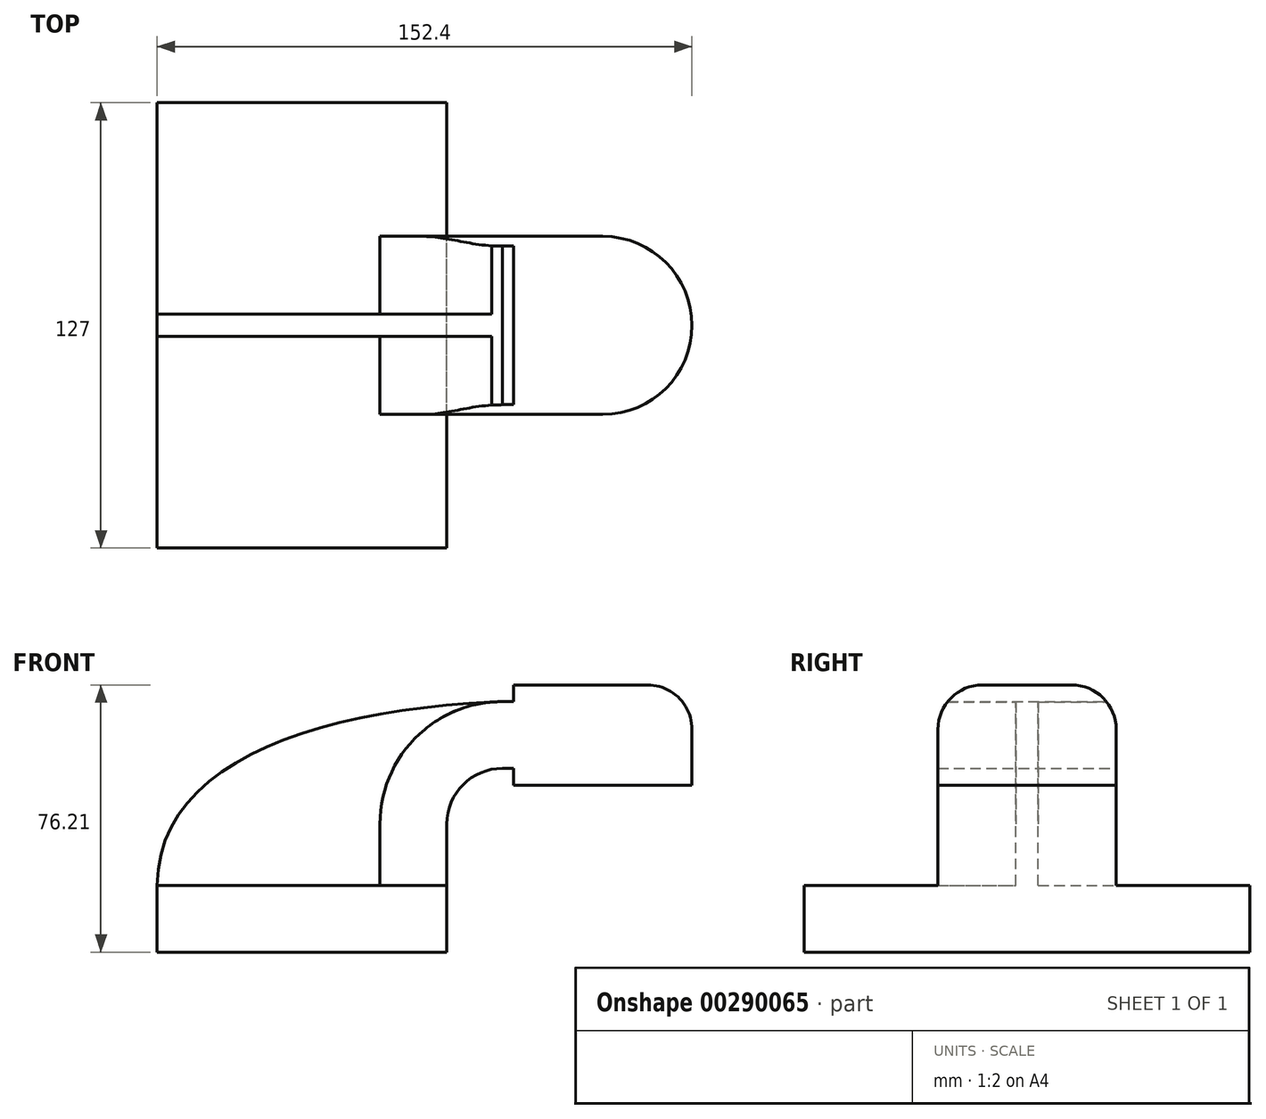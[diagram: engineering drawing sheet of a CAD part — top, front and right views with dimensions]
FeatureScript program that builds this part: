
annotation { "Feature Type Name" : "Feature", "Feature Type Description" : "" }
export const myFeature = defineFeature(function(context is Context, id is Id, definition is map)
    precondition{}
    {
        {
            var Q0;
            Q0=qCreatedBy(makeId("Front.planeOp"),FACE);
            var sketch = newSketch(context, id + "F0", { "sketchPlane" : qUnion([Q0])});
            skLineSegment(sketch, "E0.bottom", {"start": v(41.28, 9.52) * mm, "end": v(-41.28, 9.52) * mm});
            skLineSegment(sketch, "E0.top", {"start": v(41.28, -9.53) * mm, "end": v(-41.28, -9.53) * mm});
            skLineSegment(sketch, "E0.left", {"start": v(41.28, 9.52) * mm, "end": v(41.28, -9.53) * mm});
            skLineSegment(sketch, "E0.right", {"start": v(-41.28, 9.52) * mm, "end": v(-41.28, -9.53) * mm});
            skPoint(sketch, "E0.middle", {"position": v(0, 0) * mm});
            skLineSegment(sketch, "E1.bottom", {"start": v(60.33, 66.67) * mm, "end": v(111.13, 66.68) * mm});
            skLineSegment(sketch, "E1.top", {"start": v(60.33, 38.1) * mm, "end": v(111.13, 38.1) * mm});
            skLineSegment(sketch, "E1.left", {"start": v(60.33, 66.67) * mm, "end": v(60.33, 38.1) * mm});
            skLineSegment(sketch, "E1.right", {"start": v(111.13, 66.68) * mm, "end": v(111.13, 38.1) * mm});
            skPoint(sketch, "E1.middle", {"position": v(85.73, 52.39) * mm});
            skLineSegment(sketch, "E2", {"start": v(41.28, 9.52) * mm, "end": v(41.28, 27) * mm});
            skArc(sketch, "E3", {"start": v(41.28, 27) * mm, "mid": v(45.92, 38.23) * mm, "end": v(57.15, 42.88) * mm});
            skLineSegment(sketch, "E4", {"start": v(57.15, 42.88) * mm, "end": v(85.73, 42.88) * mm});
            skLineSegment(sketch, "E5.0", {"start": v(57.15, 61.93) * mm, "end": v(85.73, 61.93) * mm});
            skArc(sketch, "E5.1", {"start": v(22.23, 27) * mm, "mid": v(32.45, 51.7) * mm, "end": v(57.15, 61.93) * mm});
            skLineSegment(sketch, "E5.2", {"start": v(22.23, 9.52) * mm, "end": v(22.23, 27) * mm});
            skLineSegment(sketch, "E6", {"start": v(85.73, 38.1) * mm, "end": v(85.73, 66.67) * mm});
            skFitSpline(sketch, "E7", {"points": [v(-41.28, 9.52) * mm, v(57.15, 61.93) * mm], "startDerivative": vector(0.77, 107.77) * mm, "endDerivative": vector(154.59, 6.1) * mm});
            skSolve(sketch);
        }
        {
            var Q0;
            Q0=makeQuery(id+"F0.imprint","IMPRINT",FACE,{"disambiguationData":[TD([[makeQuery(id+"F0.imprint","IMPRINT",EDGE,{"derivedFrom":sQuery(id+"F0.wireOp",EDGE,"E0.top")}),-1.0]])]});
            extrude(context, id + "F1", {"entities" : qUnion([Q0]), "endBound" : BoundingType.SYMMETRIC, "depth" : 127 * mm});
        }
        {
            var Q0;
            {var subQ1=sQuery(id+"F0.wireOp",EDGE,"E2");Q0=makeQuery(id+"F0.imprint","IMPRINT",FACE,{"disambiguationData":[TD([[makeQuery(id+"F0.imprint","IMPRINT",EDGE,{"derivedFrom":subQ1}),1.0]])]});}
            var Q1;
            {var subQ0=sQuery(id+"F0.wireOp",EDGE,"E5.0");var subQ1=sQuery(id+"F0.wireOp",EDGE,"E1.left");var subQ2=makeQuery(id+"F0.imprint","INTERSECT",VERTEX,{"derivedFrom":[subQ1,subQ0]});Q1=makeQuery(id+"F0.imprint","IMPRINT",FACE,{"disambiguationData":[TD([[makeQuery(id+"F0.imprint","IMPRINT",EDGE,{"disambiguationData":[TD([[subQ2,-1.0]])],"derivedFrom":subQ1}),1.0]])]});}
            var Q2;
            {var subQ0=sQuery(id+"F0.wireOp",EDGE,"E1.left");var subQ1=sQuery(id+"F0.wireOp",EDGE,"E1.bottom");var subQ2=makeQuery(id+"F0.imprint","INTERSECT",VERTEX,{"derivedFrom":[subQ1,subQ0]});Q2=makeQuery(id+"F0.imprint","IMPRINT",FACE,{"disambiguationData":[TD([[makeQuery(id+"F0.imprint","IMPRINT",EDGE,{"disambiguationData":[TD([[subQ2,-1.0]])],"derivedFrom":subQ1}),-1.0]])]});}
            var Q3;
            {var subQ0=sQuery(id+"F0.wireOp",EDGE,"E1.left");var subQ1=sQuery(id+"F0.wireOp",EDGE,"E1.top");var subQ2=makeQuery(id+"F0.imprint","INTERSECT",VERTEX,{"derivedFrom":[subQ1,subQ0]});Q3=makeQuery(id+"F0.imprint","IMPRINT",FACE,{"disambiguationData":[TD([[makeQuery(id+"F0.imprint","IMPRINT",EDGE,{"disambiguationData":[TD([[subQ2,-1.0]])],"derivedFrom":subQ1}),1.0]])]});}
            extrude(context, id + "F2", {"entities" : qUnion([Q0, Q1, Q2, Q3]), "operationType" : NewBodyOperationType.ADD, "endBound" : BoundingType.SYMMETRIC, "depth" : 50.8 * mm});
        }
        {
            var Q0;
            {var subQ4=sQuery(id+"F0.wireOp",EDGE,"E1.right");Q0=makeQuery(id+"F0.imprint","IMPRINT",FACE,{"disambiguationData":[TD([[makeQuery(id+"F0.imprint","IMPRINT",EDGE,{"derivedFrom":subQ4}),-1.0]])]});}
            var Q1;
            Q1=sQuery(id+"F0.wireOp",EDGE,"E6");
            revolve(context, id + "F3", {"operationType" : NewBodyOperationType.ADD, "entities" : qUnion([Q0]), "axis" : qUnion([Q1]), "revolveType" : RevolveType.FULL});
        }
        {
            var Q0;
            {var subQ3=sQuery(id+"F0.wireOp",EDGE,"E5.2");Q0=makeQuery(id+"F0.imprint","IMPRINT",FACE,{"disambiguationData":[TD([[makeQuery(id+"F0.imprint","IMPRINT",EDGE,{"derivedFrom":subQ3}),1.0]])]});}
            extrude(context, id + "F4", {"entities" : qUnion([Q0]), "operationType" : NewBodyOperationType.ADD, "endBound" : BoundingType.SYMMETRIC, "depth" : 6.35 * mm});
        }
        {
            var Q0;
            Q0=makeQuery(id+"F3.opRevolve","SWEPT_EDGE",EDGE,{"disambiguationData":[OSD([sQuery(id+"F0.wireOp",EDGE,"E1.bottom"),sQuery(id+"F0.wireOp",EDGE,"E1.right")])]});
            fillet(context, id + "F5", {"entities" : qUnion([Q0]), "radius" : 12.7 * mm, "tangentPropagation" : true, "allowEdgeOverflow" : false});
        }
    });
